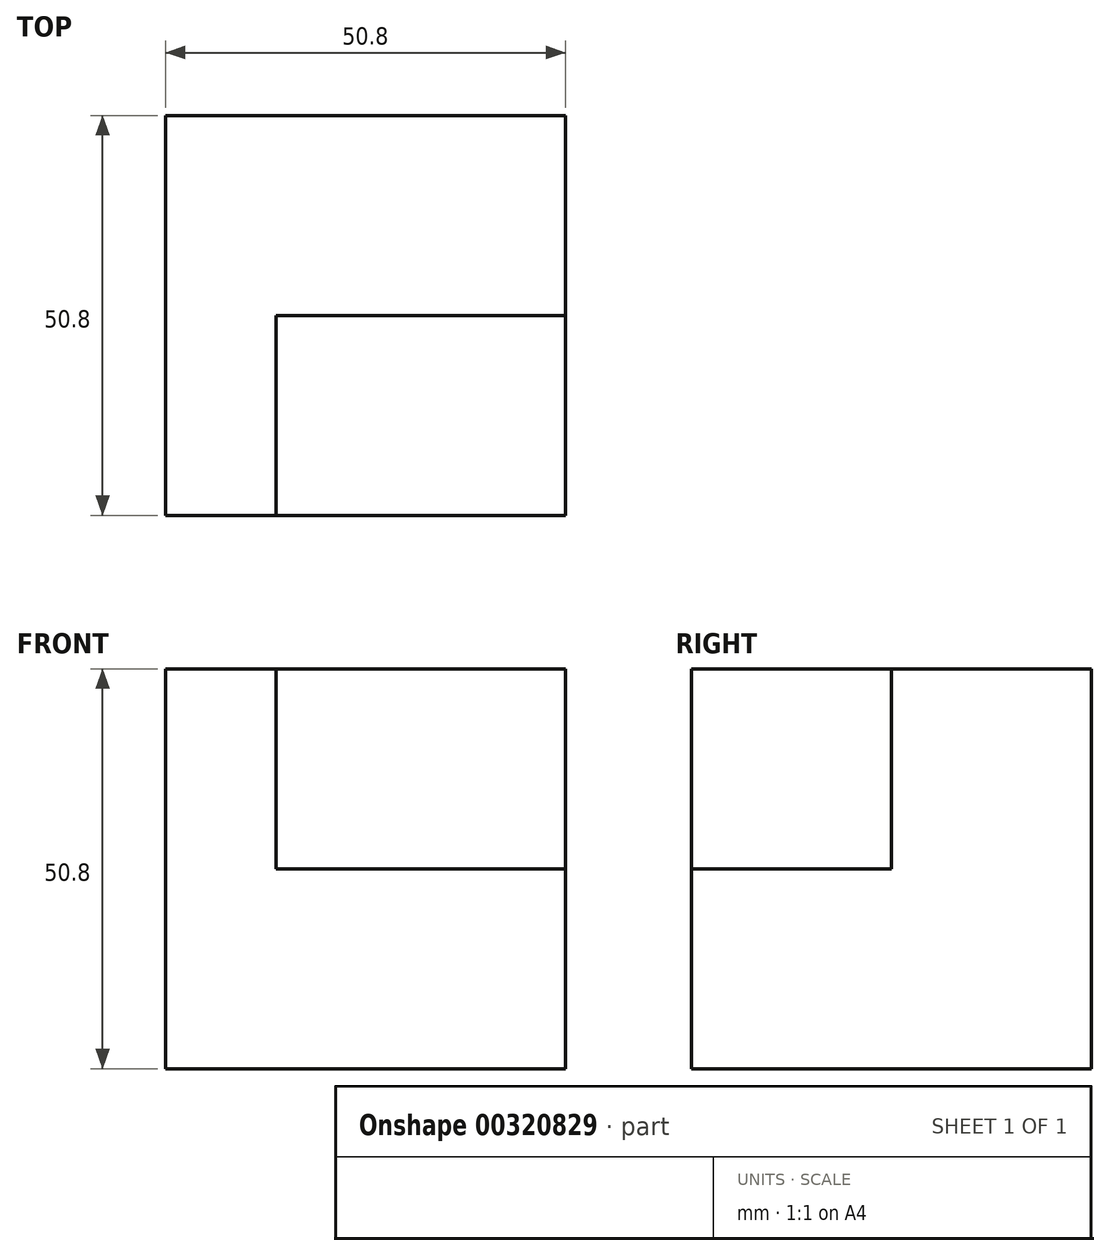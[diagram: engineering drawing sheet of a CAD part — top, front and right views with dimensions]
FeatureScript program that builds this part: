
annotation { "Feature Type Name" : "Feature", "Feature Type Description" : "" }
export const myFeature = defineFeature(function(context is Context, id is Id, definition is map)
    precondition{}
    {
        {
            var Q0;
            Q0=qCreatedBy(makeId("Front.planeOp"),FACE);
            var sketch = newSketch(context, id + "F0", { "sketchPlane" : qUnion([Q0])});
            skLineSegment(sketch, "E0", {"start": v(-0.57, -39.12) * mm, "end": v(-51.37, -39.12) * mm});
            skLineSegment(sketch, "E1", {"start": v(-51.37, -39.12) * mm, "end": v(-51.37, 11.68) * mm});
            skLineSegment(sketch, "E2", {"start": v(-51.37, 11.68) * mm, "end": v(-0.57, 11.68) * mm});
            skLineSegment(sketch, "E3", {"start": v(-0.57, 11.68) * mm, "end": v(-0.57, -39.12) * mm});
            skLineSegment(sketch, "E4.bottom", {"start": v(-37.37, 11.68) * mm, "end": v(-0.57, 11.68) * mm});
            skLineSegment(sketch, "E4.top", {"start": v(-37.37, -13.72) * mm, "end": v(-0.57, -13.72) * mm});
            skLineSegment(sketch, "E4.left", {"start": v(-37.37, 11.68) * mm, "end": v(-37.37, -13.72) * mm});
            skLineSegment(sketch, "E4.right", {"start": v(-0.57, 11.68) * mm, "end": v(-0.57, -13.72) * mm});
            skSolve(sketch);
        }
        {
            var Q0;
            Q0=makeQuery(id+"F0.imprint","IMPRINT",FACE,{"disambiguationData":[TD([[makeQuery(id+"F0.imprint","IMPRINT",EDGE,{"derivedFrom":sQuery(id+"F0.wireOp",EDGE,"E0")}),-1.0]])]});
            extrude(context, id + "F1", {"entities" : qUnion([Q0]), "depth" : 50.8 * mm});
        }
        {
            var Q0;
            Q0=makeQuery(id+"F1.opExtrude","SWEPT_FACE",FACE,{"disambiguationData":[OSD([sQuery(id+"F0.wireOp",EDGE,"E4.top")])]});
            var sketch = newSketch(context, id + "F2", { "sketchPlane" : qUnion([Q0])});
            skLineSegment(sketch, "E5.bottom", {"start": v(-37.37, 0) * mm, "end": v(0.73, 0) * mm});
            skLineSegment(sketch, "E5.top", {"start": v(-37.37, -25.4) * mm, "end": v(0.73, -25.4) * mm});
            skLineSegment(sketch, "E5.left", {"start": v(-37.37, 0) * mm, "end": v(-37.37, -25.4) * mm});
            skLineSegment(sketch, "E5.right", {"start": v(0.73, 0) * mm, "end": v(0.73, -25.4) * mm});
            skSolve(sketch);
        }
        {
            var Q0;
            {var subQ4=sQuery(id+"F2.wireOp",EDGE,"E5.left");Q0=makeQuery(id+"F2.imprint","IMPRINT",FACE,{"disambiguationData":[TD([[makeQuery(id+"F2.imprint","IMPRINT",EDGE,{"derivedFrom":subQ4}),-1.0]])]});}
            extrude(context, id + "F3", {"entities" : qUnion([Q0]), "operationType" : NewBodyOperationType.ADD, "depth" : 25.4 * mm});
        }
    });
